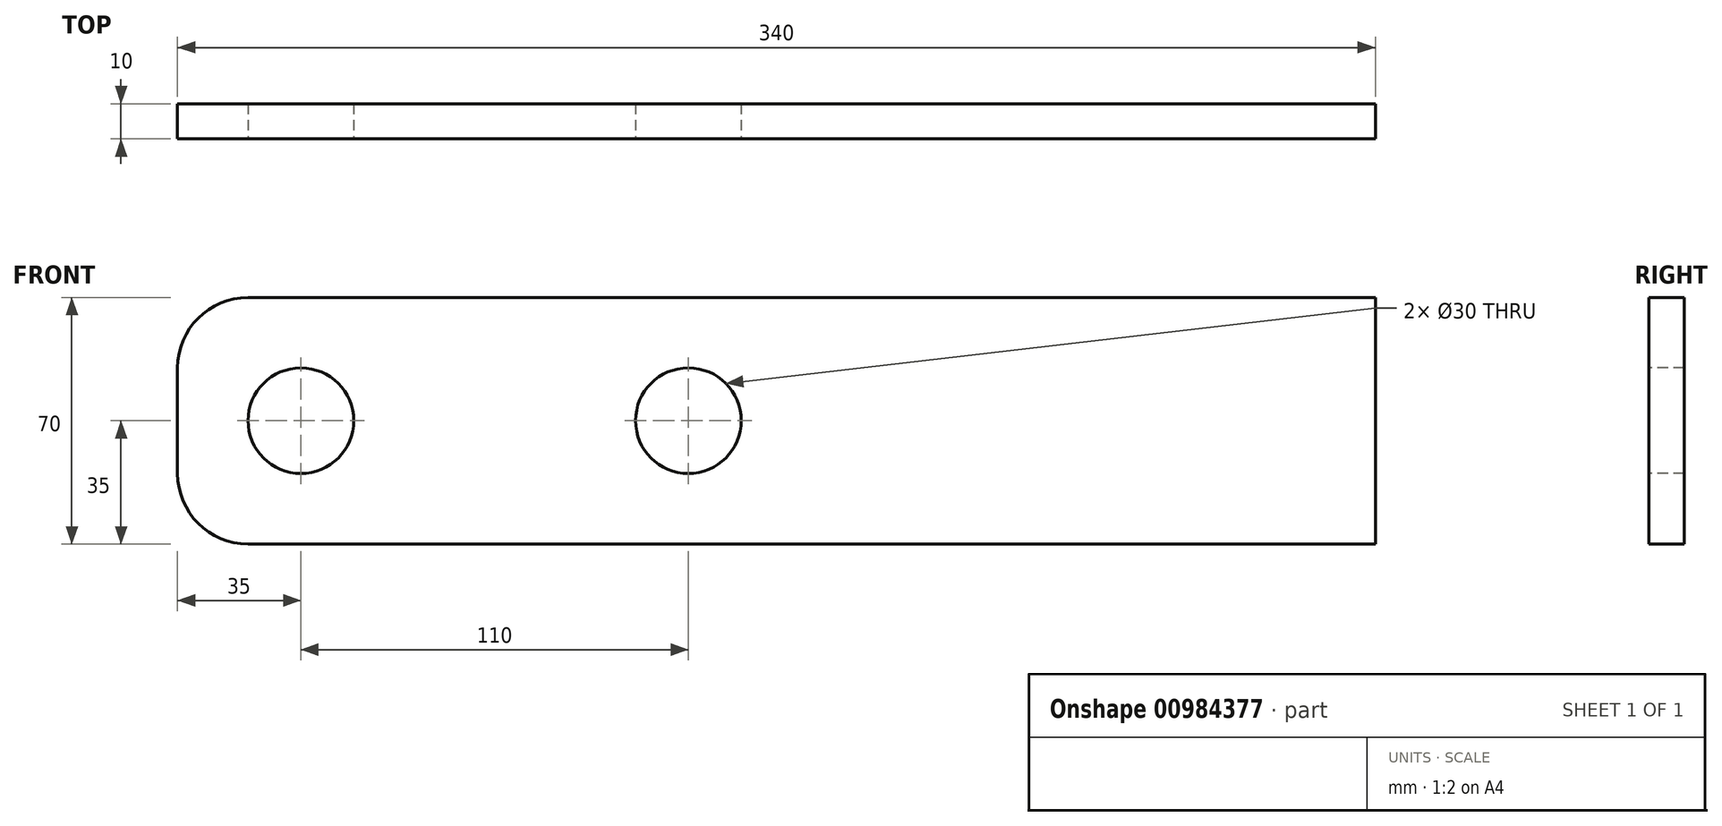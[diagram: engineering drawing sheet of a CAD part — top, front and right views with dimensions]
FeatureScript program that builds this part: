
annotation { "Feature Type Name" : "Feature", "Feature Type Description" : "" }
export const myFeature = defineFeature(function(context is Context, id is Id, definition is map)
    precondition{}
    {
        {
            var Q0;
            Q0=qCreatedBy(makeId("Front.planeOp"),FACE);
            var sketch = newSketch(context, id + "F0", { "sketchPlane" : qUnion([Q0])});
            skLineSegment(sketch, "E0.bottom", {"start": v(170, -35) * mm, "end": v(-170, -35) * mm});
            skLineSegment(sketch, "E0.top", {"start": v(170, 35) * mm, "end": v(-170, 35) * mm});
            skLineSegment(sketch, "E0.left", {"start": v(170, -35) * mm, "end": v(170, 35) * mm});
            skLineSegment(sketch, "E0.right", {"start": v(-170, -35) * mm, "end": v(-170, 35) * mm});
            skPoint(sketch, "E0.middle", {"position": v(0, 0) * mm});
            skSolve(sketch);
        }
        {
            var Q0;
            Q0=qSketchRegion(id+"F0",true);
            extrude(context, id + "F1", {"entities" : qUnion([Q0]), "depth" : 10 * mm, "offsetDistance" : 25 * mm});
        }
        {
            var Q0;
            Q0=makeQuery(id+"F1.opExtrude","SWEPT_EDGE",EDGE,{"disambiguationData":[OSD([sQuery(id+"F0.wireOp",EDGE,"E0.top"),sQuery(id+"F0.wireOp",EDGE,"E0.right")])]});
            var Q1;
            Q1=makeQuery(id+"F1.opExtrude","SWEPT_EDGE",EDGE,{"disambiguationData":[OSD([sQuery(id+"F0.wireOp",EDGE,"E0.bottom"),sQuery(id+"F0.wireOp",EDGE,"E0.right")])]});
            fillet(context, id + "F2", {"entities" : qUnion([Q0, Q1]), "radius" : 20 * mm, "tangentPropagation" : true, "allowEdgeOverflow" : false});
        }
        {
            var Q0;
            Q0=qCreatedBy(makeId("Front.planeOp"),FACE);
            var sketch = newSketch(context, id + "F3", { "sketchPlane" : qUnion([Q0])});
            skCircle(sketch, "E1", {"center": v(-135, 0) * mm, "radius": 15 * mm});
            skCircle(sketch, "E2", {"center": v(-25, 0) * mm, "radius": 15 * mm});
            skSolve(sketch);
        }
        {
            var Q0;
            Q0=qSketchRegion(id+"F3",true);
            extrude(context, id + "F4", {"entities" : qUnion([Q0]), "operationType" : NewBodyOperationType.REMOVE, "endBound" : BoundingType.THROUGH_ALL, "oppositeDirection" : true, "depth" : 25 * mm, "offsetDistance" : 25 * mm, "hasSecondDirection" : true, "secondDirectionOppositeDirection" : false, "secondDirectionDepth" : 25 * mm});
        }
    });
